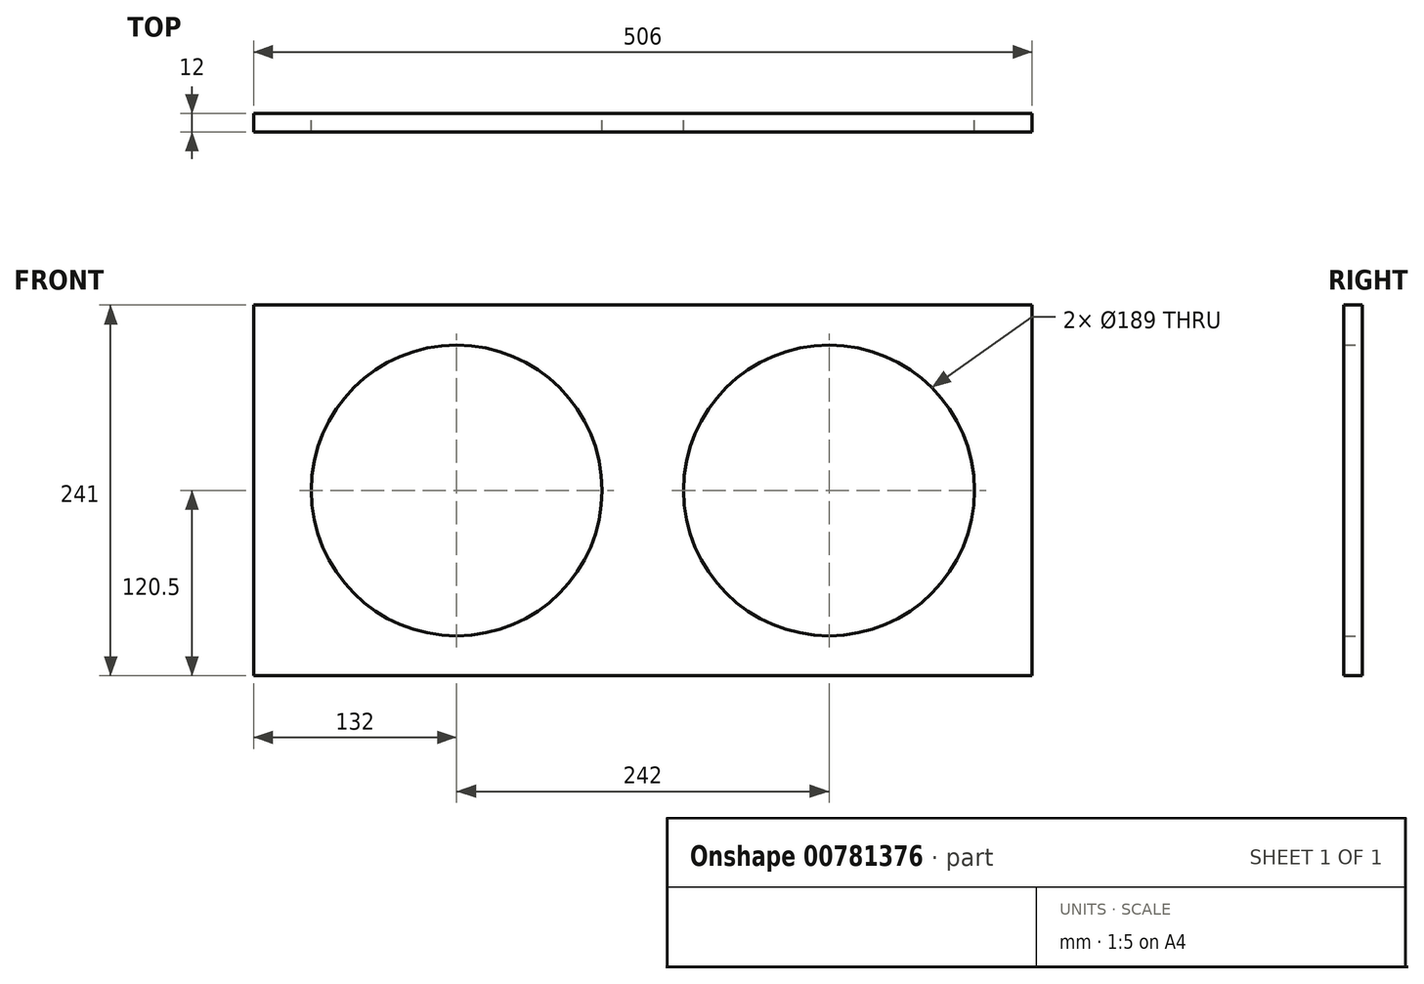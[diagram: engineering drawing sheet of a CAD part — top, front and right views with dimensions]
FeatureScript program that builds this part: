
annotation { "Feature Type Name" : "Feature", "Feature Type Description" : "" }
export const myFeature = defineFeature(function(context is Context, id is Id, definition is map)
    precondition{}
    {
        {
            var Q0;
            Q0=qCreatedBy(makeId("Front.planeOp"),FACE);
            var sketch = newSketch(context, id + "F0", { "sketchPlane" : qUnion([Q0])});
            skLineSegment(sketch, "E0.bottom", {"start": v(-253, -120.5) * mm, "end": v(253, -120.5) * mm});
            skLineSegment(sketch, "E0.top", {"start": v(-253, 120.5) * mm, "end": v(253, 120.5) * mm});
            skLineSegment(sketch, "E0.left", {"start": v(-253, -120.5) * mm, "end": v(-253, 120.5) * mm});
            skLineSegment(sketch, "E0.right", {"start": v(253, -120.5) * mm, "end": v(253, 120.5) * mm});
            skPoint(sketch, "E0.middle", {"position": v(0, 0) * mm});
            skCircle(sketch, "E1", {"center": v(121, 0) * mm, "radius": 94.5 * mm});
            skCircle(sketch, "E2", {"center": v(-121, 0) * mm, "radius": 94.5 * mm});
            skCircle(sketch, "E3", {"center": v(-121, 0) * mm, "radius": 111 * mm});
            skCircle(sketch, "E4", {"center": v(121, 0) * mm, "radius": 111 * mm});
            skSolve(sketch);
        }
        {
            var Q0;
            Q0=makeQuery(id+"F0.imprint","IMPRINT",FACE,{"disambiguationData":[TD([[makeQuery(id+"F0.imprint","IMPRINT",EDGE,{"derivedFrom":sQuery(id+"F0.wireOp",EDGE,"E0.bottom")}),1.0]])]});
            var Q1;
            Q1=makeQuery(id+"F0.imprint","IMPRINT",FACE,{"disambiguationData":[TD([[makeQuery(id+"F0.imprint","IMPRINT",EDGE,{"derivedFrom":sQuery(id+"F0.wireOp",EDGE,"E2")}),-1.0]])]});
            var Q2;
            Q2=makeQuery(id+"F0.imprint","IMPRINT",FACE,{"disambiguationData":[TD([[makeQuery(id+"F0.imprint","IMPRINT",EDGE,{"derivedFrom":sQuery(id+"F0.wireOp",EDGE,"E1")}),-1.0]])]});
            extrude(context, id + "F1", {"entities" : qUnion([Q0, Q1, Q2]), "depth" : 12 * mm, "offsetDistance" : 25 * mm});
        }
    });
